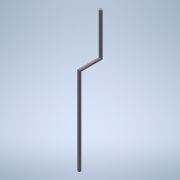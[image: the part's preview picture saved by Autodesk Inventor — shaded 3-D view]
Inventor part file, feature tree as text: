
AUTODESK INVENTOR PART (.ipt)
format: ipt  version: 2022 (Build 260153000, 153)  size: 111,104 bytes
history: native  units: in
note: dims shown in document units (in); Inventor stores cm internally (conversion verified against a paired STEP export)
features: sketch x3, sweep x1, extrude x1
ambient origin geometry x8: Origin, YZ Plane, XZ Plane, XY Plane, X Axis, Y Axis, Z Axis, Center Point
bodies: Volumenkörper1 (feature_tree)
feature tree (5):
  sweep  "Sweeping1"
  extrude  "Extrusion1"  TaperAngle=0.0deg  [1 undecoded]
  sketch  "Skizze1"  dims[d0=0.5906in d1=0.2953in]
  sketch  "Skizze2"  dims[d2=0.0394in d3=0.0in d4=0.0in]
  sketch  "Skizze3"  dims[d5=45.0deg d6=0.0in d7=0.0in]
note: 1 required parameter value undecoded (feature->parameter linkage not recoverable at this tier; creation-order binding heuristic only, values carry confidence <= 0.55)
